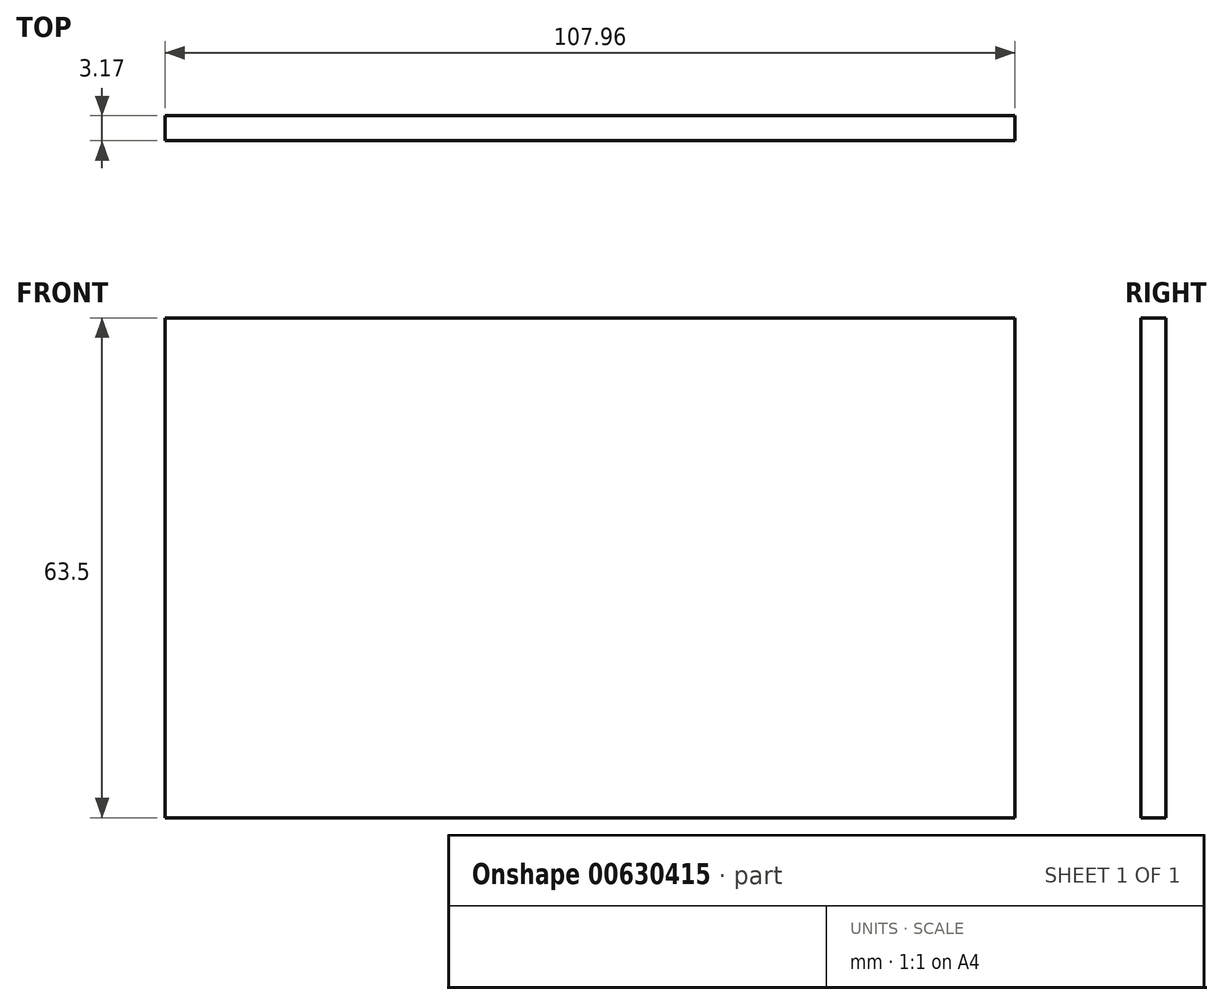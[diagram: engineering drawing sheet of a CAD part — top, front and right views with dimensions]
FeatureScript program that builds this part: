
annotation { "Feature Type Name" : "Feature", "Feature Type Description" : "" }
export const myFeature = defineFeature(function(context is Context, id is Id, definition is map)
    precondition{}
    {
        {
            var Q0;
            Q0=qCreatedBy(makeId("Front.planeOp"),FACE);
            var sketch = newSketch(context, id + "F0", { "sketchPlane" : qUnion([Q0])});
            skLineSegment(sketch, "E0.bottom", {"start": v(53.98, 31.75) * mm, "end": v(-53.97, 31.75) * mm});
            skLineSegment(sketch, "E0.top", {"start": v(53.97, -31.75) * mm, "end": v(-53.98, -31.75) * mm});
            skLineSegment(sketch, "E0.left", {"start": v(53.98, 31.75) * mm, "end": v(53.97, -31.75) * mm});
            skLineSegment(sketch, "E0.right", {"start": v(-53.97, 31.75) * mm, "end": v(-53.98, -31.75) * mm});
            skPoint(sketch, "E0.middle", {"position": v(0, 0) * mm});
            skSolve(sketch);
        }
        {
            var Q0;
            Q0=makeQuery(id+"F0.imprint","IMPRINT",FACE,{"disambiguationData":[TD([[makeQuery(id+"F0.imprint","IMPRINT",EDGE,{"derivedFrom":sQuery(id+"F0.wireOp",EDGE,"E0.bottom")}),1.0]])]});
            extrude(context, id + "F1", {"entities" : qUnion([Q0]), "depth" : 3.17 * mm, "offsetDistance" : 25.4 * mm});
        }
    });
